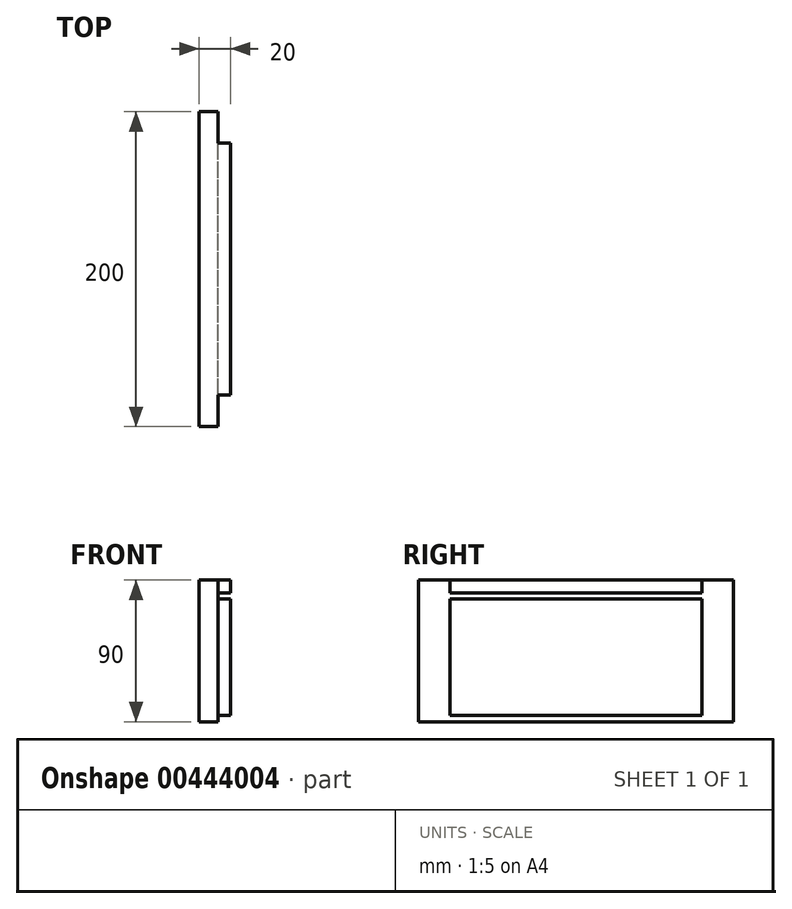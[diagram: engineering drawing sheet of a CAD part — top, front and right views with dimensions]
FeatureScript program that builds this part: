
annotation { "Feature Type Name" : "Feature", "Feature Type Description" : "" }
export const myFeature = defineFeature(function(context is Context, id is Id, definition is map)
    precondition{}
    {
        {
            var Q0;
            Q0=qCreatedBy(makeId("Right.planeOp"),FACE);
            var sketch = newSketch(context, id + "F0", { "sketchPlane" : qUnion([Q0])});
            skLineSegment(sketch, "E0.bottom", {"start": v(-93.06, 19.76) * mm, "end": v(106.94, 19.76) * mm});
            skLineSegment(sketch, "E0.top", {"start": v(-93.06, -70.24) * mm, "end": v(106.94, -70.24) * mm});
            skLineSegment(sketch, "E0.left", {"start": v(-93.06, 19.76) * mm, "end": v(-93.06, -70.24) * mm});
            skLineSegment(sketch, "E0.right", {"start": v(106.94, 19.76) * mm, "end": v(106.94, -70.24) * mm});
            skLineSegment(sketch, "E1", {"start": v(-73.06, 11.76) * mm, "end": v(86.94, 11.76) * mm});
            skLineSegment(sketch, "E2", {"start": v(-73.06, 19.76) * mm, "end": v(-73.06, 11.76) * mm});
            skLineSegment(sketch, "E3", {"start": v(86.94, 19.76) * mm, "end": v(86.94, 11.76) * mm});
            skPoint(sketch, "E4.orphan", {"position": v(-93.06, 11.76) * mm});
            skLineSegment(sketch, "E5", {"start": v(-73.06, -66.24) * mm, "end": v(86.94, -66.24) * mm});
            skLineSegment(sketch, "E6", {"start": v(-73.06, 7.76) * mm, "end": v(86.94, 7.76) * mm});
            skLineSegment(sketch, "E7.trimOffspring", {"start": v(-73.06, 7.76) * mm, "end": v(-73.06, -66.24) * mm});
            skLineSegment(sketch, "E8.trimOffspring", {"start": v(86.94, 7.76) * mm, "end": v(86.94, -66.24) * mm});
            skPoint(sketch, "E9.orphan", {"position": v(86.94, -70.24) * mm});
            skPoint(sketch, "E10.orphan", {"position": v(-73.06, -70.24) * mm});
            skSolve(sketch);
        }
        {
            var Q0;
            Q0=makeQuery(id+"F0.imprint","IMPRINT",FACE,{"disambiguationData":[TD([[makeQuery(id+"F0.imprint","IMPRINT",EDGE,{"derivedFrom":sQuery(id+"F0.wireOp",EDGE,"E0.top")}),1.0]])]});
            extrude(context, id + "F1", {"entities" : qUnion([Q0]), "depth" : 12 * mm});
        }
        {
            var Q0;
            Q0=makeQuery(id+"F0.imprint","IMPRINT",FACE,{"disambiguationData":[TD([[makeQuery(id+"F0.imprint","IMPRINT",EDGE,{"derivedFrom":sQuery(id+"F0.wireOp",EDGE,"E1")}),1.0]])]});
            var Q1;
            Q1=makeQuery(id+"F0.imprint","IMPRINT",FACE,{"disambiguationData":[TD([[makeQuery(id+"F0.imprint","IMPRINT",EDGE,{"derivedFrom":sQuery(id+"F0.wireOp",EDGE,"E5")}),1.0]])]});
            extrude(context, id + "F2", {"entities" : qUnion([Q0, Q1]), "operationType" : NewBodyOperationType.ADD, "depth" : 20 * mm});
        }
    });
